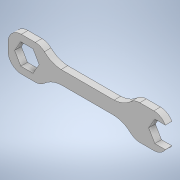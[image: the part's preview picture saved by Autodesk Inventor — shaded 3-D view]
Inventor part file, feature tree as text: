
AUTODESK INVENTOR PART (.ipt)
format: ipt  version: 2020.2 (Build 242310000, 310)  size: 160,768 bytes
history: native  units: in
note: dims shown in document units (in); Inventor stores cm internally (conversion verified against a paired STEP export)
features: extrude x1, sketch x1
ambient origin geometry x8: Origin, YZ Plane, XZ Plane, XY Plane, X Axis, Y Axis, Z Axis, Center Point
bodies: Solid1 (feature_tree)
feature tree (2):
  extrude  "Extrusion1"  Depth=0.8in
  sketch  "Sketch1"  dims[d3=0.25in d4=0.8in d8=1.75in d10=1.0in d11=1.0in d15=0.5in d16=0.5in d17=0.5in d18=0.25in d19=0.0in]
